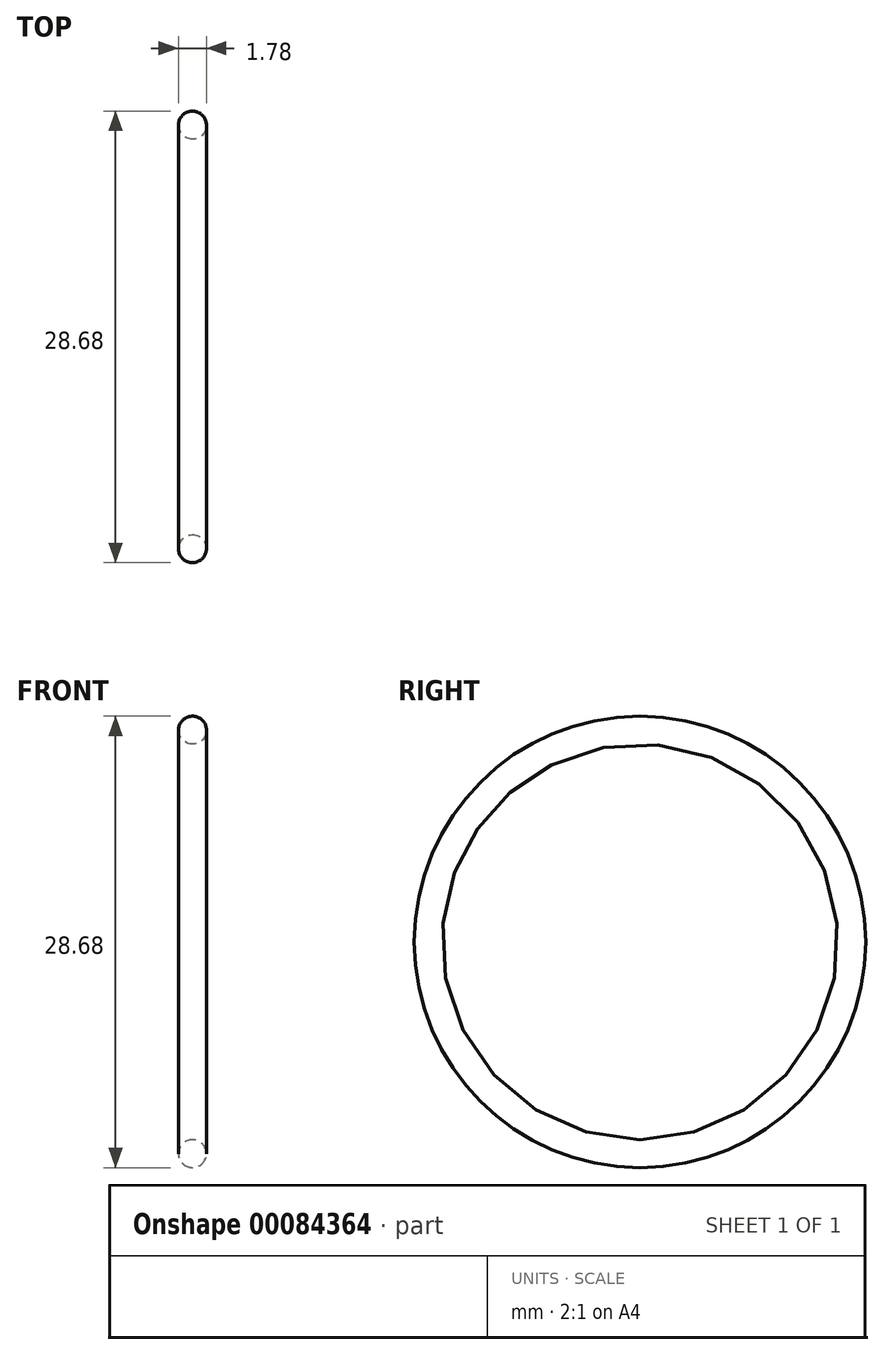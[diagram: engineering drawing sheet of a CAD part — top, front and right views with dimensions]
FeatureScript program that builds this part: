
annotation { "Feature Type Name" : "Feature", "Feature Type Description" : "" }
export const myFeature = defineFeature(function(context is Context, id is Id, definition is map)
    precondition{}
    {
        {
            var Q0;
            Q0=qCreatedBy(makeId("Front.planeOp"),FACE);
            var sketch = newSketch(context, id + "F0", { "sketchPlane" : qUnion([Q0])});
            skLineSegment(sketch, "E0", {"start": v(0, 0) * mm, "end": v(-6.06, 0) * mm, "construction": true});
            skCircle(sketch, "E1", {"center": v(0, 13.45) * mm, "radius": 0.89 * mm});
            skSolve(sketch);
        }
        {
            var Q0;
            Q0=makeQuery(id+"F0.imprint","IMPRINT",FACE,{"disambiguationData":[TD([[makeQuery(id+"F0.imprint","IMPRINT",EDGE,{"derivedFrom":sQuery(id+"F0.wireOp",EDGE,"E1")}),1.0]])]});
            var Q1;
            Q1=sQuery(id+"F0.wireOp",EDGE,"E0");
            revolve(context, id + "F1", {"entities" : qUnion([Q0]), "axis" : qUnion([Q1]), "revolveType" : RevolveType.FULL});
        }
    });
